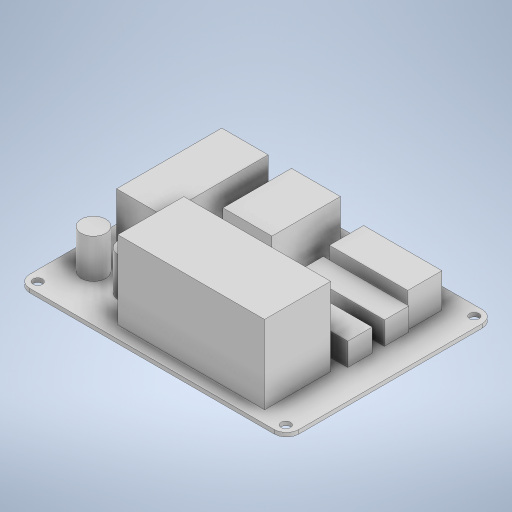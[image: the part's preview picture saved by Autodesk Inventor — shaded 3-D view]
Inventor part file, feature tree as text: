
AUTODESK INVENTOR PART (.ipt)
format: ipt  version: 2023 (Build 270158000, 158)  size: 362,496 bytes
history: native  units: in
note: dims shown in document units (in); Inventor stores cm internally (conversion verified against a paired STEP export)
features: extrude x9, sketch x6, fillet x1
ambient origin geometry x8: Origin, YZ Plane, XZ Plane, XY Plane, X Axis, Y Axis, Z Axis, Center Point
bodies: Solid1 (feature_tree)
feature tree (16):
  extrude  "Extrusion1"  Depth=4.3307in
  fillet  "Fillet1"  Radius=0.063in
  extrude  "Extrusion2"  Depth=0.1969in
  extrude  "Extrusion3"  Depth=0.1535in
  extrude  "Extrusion4"  Depth=0.1693in
  extrude  "Extrusion5"  Depth=0.1575in
  sketch  "Sketch6"  dims[d12=0.1575in d13=0.1693in d14=0.1575in d15=0.1693in d16=0.1575in d17=0.0in d18=0.0in d19=0.3976in d20=0.3976in d21=0.75in d22=0.75in d23=0.4744in d24=0.5945in d25=0.6299in d26=0.0in d27=2.3622in d28=1.063in d29=0.1969in d30=0.5512in d31=1.2598in d32=0.0in d33=0.374in d34=0.748in d35=1.6929in d36=0.4331in d37=0.8661in d38=0.0in d39=0.7874in d40=1.1024in d41=0.3543in d42=0.0787in d43=0.4724in d44=1.0236in d45=0.2362in d46=0.2953in d47=1.378in d48=1.378in d49=0.3937in d50=0.3937in d51=0.1969in d52=0.4724in d53=0.4724in d54=0.1969in d55=1.2598in d56=0.5512in d57=0.3346in d58=0.5118in d59=0.7874in d60=0.0in d61=0.4724in d62=0.0in d63=0.3661in d64=0.0in d65=0.5512in d66=0.0in]
  extrude  "Extrusion6"  Depth=0.5512in
  extrude  "Extrusion7"  Depth=0.1575in
  extrude  "Extrusion8"  Depth=0.5512in
  extrude  "Extrusion9"  Depth=0.1575in
  sketch  "Sketch1"  dims[d0=3.3465in d1=4.3307in d2=0.063in d3=0.0in]
  sketch  "Sketch2"  dims[d4=0.1969in d5=0.1535in]
  sketch  "Sketch3"  dims[d6=0.1535in d7=0.1535in]
  sketch  "Sketch4"  dims[d8=0.1535in d9=0.1693in]
  sketch  "Sketch5"  dims[d10=0.1575in d11=0.1693in]
